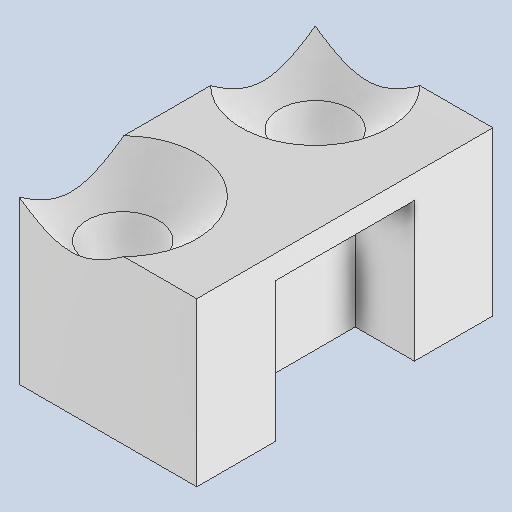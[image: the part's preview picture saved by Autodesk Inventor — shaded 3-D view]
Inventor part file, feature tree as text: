
AUTODESK INVENTOR PART (.ipt)
format: ipt  version: 2025 (Build 290162010, 162A)  size: 165,376 bytes
history: native  units: mm
features: sketch x3, reference x3, other x3, extrude x2, hole x1
ambient origin geometry x8: Origin, YZ Plane, XZ Plane, XY Plane, X Axis, Y Axis, Z Axis, Center Point
bodies: Volumenkörper1 (feature_tree)
feature tree (12):
  extrude  "Extrusion1"  Depth=10.0mm
  extrude  "Extrusion2"  Depth=5.5mm TaperAngle=0.0deg
  hole  "Bohrung1"  [1 undecoded]
  sketch  "Skizze1"  dims[d0=6.0mm d1=10.0mm]
  reference  "Referenz1"
  reference  "Referenz2"
  reference  "Referenz3"
  sketch  "Skizze2"  dims[d2=6.0mm d3=5.5mm d4=0.0mm]
  sketch  "Skizze3"  dims[d5=4.7mm d6=4.7mm d7=2.0mm d8=0.0mm d9=1.75mm d10=2.4mm d11=6.0mm d12=5.0mm d13=2.0mm d14=90.0deg d15=8.0mm d16=20.594885mm]
  other  "<userpath>\Documents\Inventor\Krandemonstrator\Schlitten.iam"
  other  "Schlitten.iam"
  other  "SchubstangeA:1"
note: 1 required parameter value undecoded (feature->parameter linkage not recoverable at this tier; creation-order binding heuristic only, values carry confidence <= 0.55)
